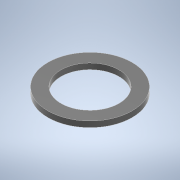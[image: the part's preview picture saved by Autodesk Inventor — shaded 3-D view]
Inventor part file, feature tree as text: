
AUTODESK INVENTOR PART (.ipt)
format: ipt  version: 2021 (Build 250183000, 183)  size: 99,840 bytes
history: native  units: mm
features: extrude x1, sketch x1
ambient origin geometry x8: Origin, YZ Plane, XZ Plane, XY Plane, X Axis, Y Axis, Z Axis, Center Point
bodies: Solid1 (feature_tree)
feature tree (2):
  extrude  "Extrusion1"  Depth=1.2mm
  sketch  "Sketch1"  dims[d0=17.5mm d1=12.1mm d2=1.2mm d3=0.0mm]
